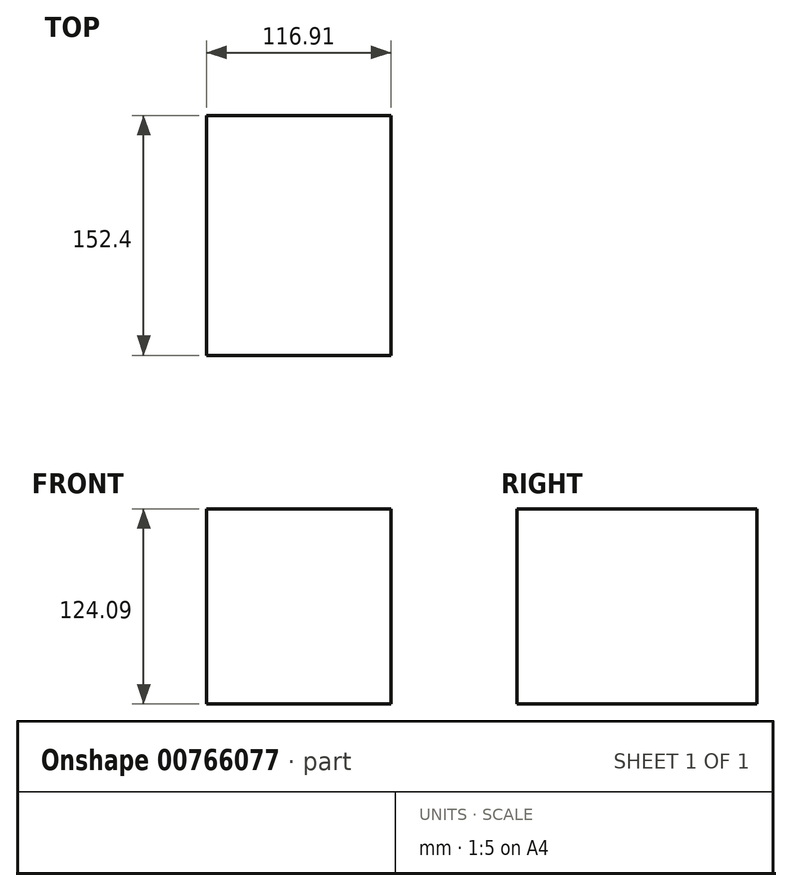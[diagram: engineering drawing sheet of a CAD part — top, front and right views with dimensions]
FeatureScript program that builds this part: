
annotation { "Feature Type Name" : "Feature", "Feature Type Description" : "" }
export const myFeature = defineFeature(function(context is Context, id is Id, definition is map)
    precondition{}
    {
        {
            var Q0;
            Q0=qCreatedBy(makeId("Front.planeOp"),FACE);
            var sketch = newSketch(context, id + "F0", { "sketchPlane" : qUnion([Q0])});
            skLineSegment(sketch, "E0.bottom", {"start": v(48.81, 66.04) * mm, "end": v(-68.1, 66.04) * mm});
            skLineSegment(sketch, "E0.top", {"start": v(48.81, -58.05) * mm, "end": v(-68.1, -58.05) * mm});
            skLineSegment(sketch, "E0.left", {"start": v(48.81, 66.04) * mm, "end": v(48.81, -58.05) * mm});
            skLineSegment(sketch, "E0.right", {"start": v(-68.1, 66.04) * mm, "end": v(-68.1, -58.05) * mm});
            skPoint(sketch, "E0.middle", {"position": v(-9.64, 4) * mm});
            skSolve(sketch);
        }
        {
            var Q0;
            Q0=makeQuery(id+"F0.imprint","IMPRINT",FACE,{"disambiguationData":[TD([[makeQuery(id+"F0.imprint","IMPRINT",EDGE,{"derivedFrom":sQuery(id+"F0.wireOp",EDGE,"E0.bottom")}),1.0]])]});
            extrude(context, id + "F1", {"entities" : qUnion([Q0]), "depth" : 50.8 * mm, "offsetDistance" : 25.4 * mm});
        }
        {
            var Q0;
            Q0=makeQuery(id+"F1.opExtrude","CAP_FACE",FACE,{"disambiguationData":[OSD([sQuery(id+"F0.wireOp",EDGE,"E0.bottom"),sQuery(id+"F0.wireOp",EDGE,"E0.top"),sQuery(id+"F0.wireOp",EDGE,"E0.left"),sQuery(id+"F0.wireOp",EDGE,"E0.right")])],"isStart":false});
            extrude(context, id + "F2", {"entities" : qUnion([Q0]), "operationType" : NewBodyOperationType.ADD, "depth" : 101.6 * mm, "offsetDistance" : 25.4 * mm});
        }
    });
